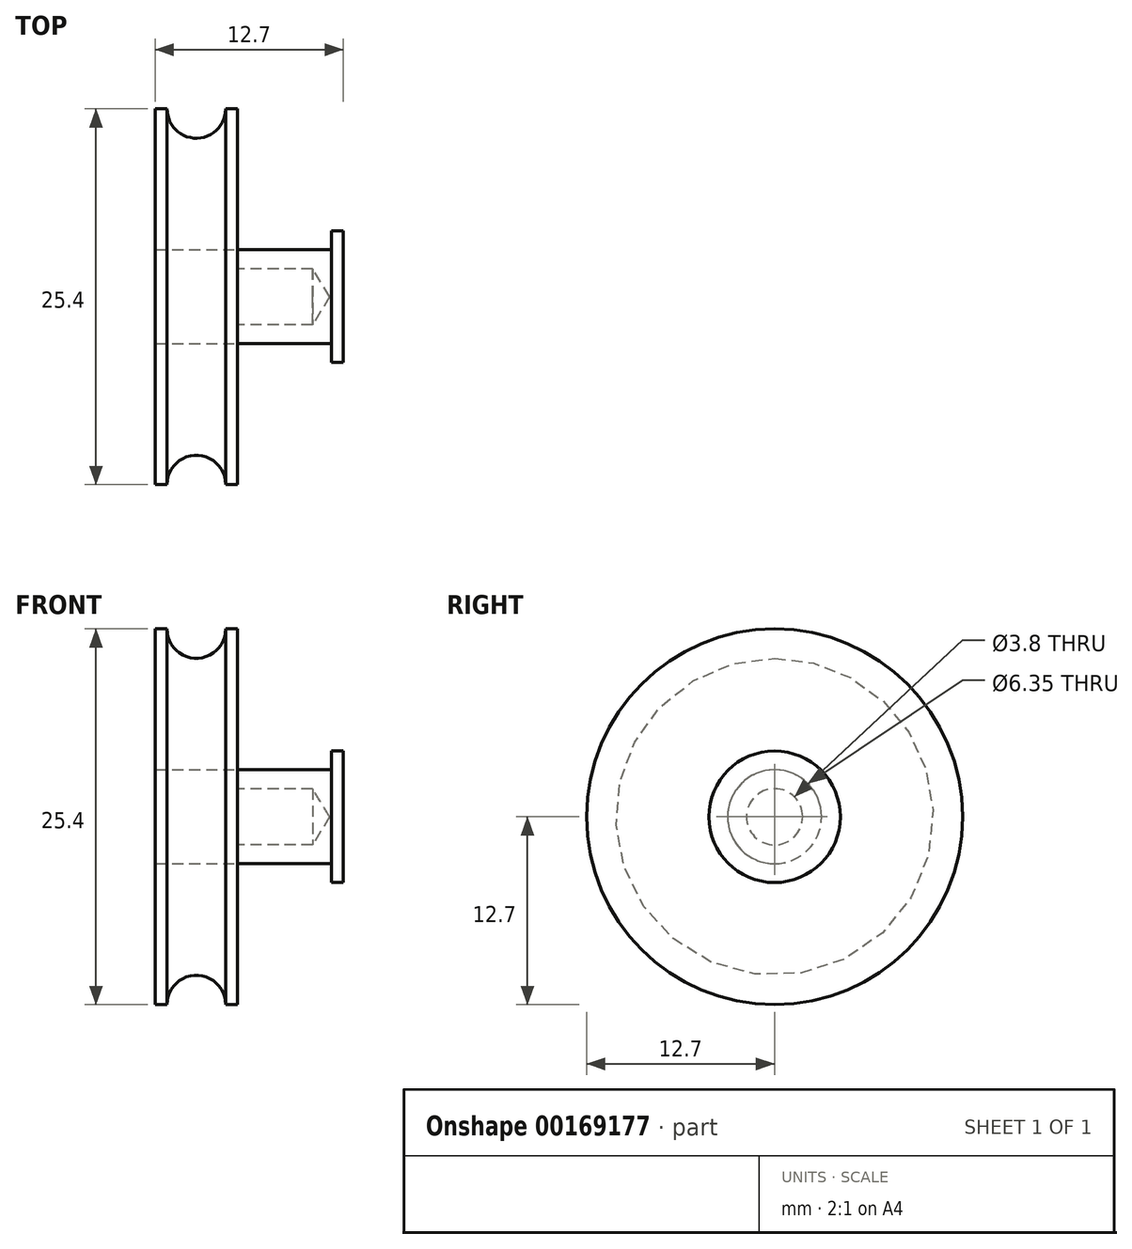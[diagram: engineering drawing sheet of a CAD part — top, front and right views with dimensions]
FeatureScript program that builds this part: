
annotation { "Feature Type Name" : "Feature", "Feature Type Description" : "" }
export const myFeature = defineFeature(function(context is Context, id is Id, definition is map)
    precondition{}
    {
        {
            var Q0;
            Q0=qCreatedBy(makeId("Front.planeOp"),FACE);
            var sketch = newSketch(context, id + "F0", { "sketchPlane" : qUnion([Q0])});
            skLineSegment(sketch, "E0.bottom", {"start": v(0, 0) * mm, "end": v(5.56, 0) * mm});
            skLineSegment(sketch, "E0.top", {"start": v(0, 12.7) * mm, "end": v(0.8, 12.7) * mm});
            skLineSegment(sketch, "E0.left", {"start": v(0, 0) * mm, "end": v(0, 12.7) * mm});
            skLineSegment(sketch, "E0.right", {"start": v(5.56, 0) * mm, "end": v(5.56, 12.7) * mm});
            skLineSegment(sketch, "E1.trimOffspring", {"start": v(4.76, 12.7) * mm, "end": v(5.56, 12.7) * mm});
            skArc(sketch, "E2", {"start": v(0.8, 12.7) * mm, "mid": v(2.78, 10.72) * mm, "end": v(4.76, 12.7) * mm});
            skSolve(sketch);
        }
        {
            var Q0;
            Q0=makeQuery(id+"F0.imprint","IMPRINT",FACE,{"disambiguationData":[TD([[makeQuery(id+"F0.imprint","IMPRINT",EDGE,{"derivedFrom":sQuery(id+"F0.wireOp",EDGE,"E0.bottom")}),1.0]])]});
            var Q1;
            Q1=sQuery(id+"F0.wireOp",EDGE,"E0.bottom");
            revolve(context, id + "F1", {"entities" : qUnion([Q0]), "axis" : qUnion([Q1]), "revolveType" : RevolveType.FULL});
        }
        {
            var Q0;
            Q0=makeQuery(id+"F1.opRevolve","SWEPT_FACE",FACE,{"disambiguationData":[OSD([sQuery(id+"F0.wireOp",EDGE,"E0.right")])]});
            var sketch = newSketch(context, id + "F2", { "sketchPlane" : qUnion([Q0])});
            skCircle(sketch, "E3", {"center": v(0, 0) * mm, "radius": 3.18 * mm});
            skSolve(sketch);
        }
        {
            var Q0;
            Q0=makeQuery(id+"F2.imprint","IMPRINT",FACE,{"disambiguationData":[TD([[makeQuery(id+"F2.imprint","IMPRINT",EDGE,{"derivedFrom":sQuery(id+"F2.wireOp",EDGE,"E3")}),1.0]])]});
            extrude(context, id + "F3", {"entities" : qUnion([Q0]), "operationType" : NewBodyOperationType.REMOVE, "endBound" : BoundingType.UP_TO_NEXT, "oppositeDirection" : true, "depth" : 25.4 * mm});
        }
        {
            var Q0;
            Q0=makeQuery(id+"F2.imprint","IMPRINT",FACE,{"disambiguationData":[TD([[makeQuery(id+"F2.imprint","IMPRINT",EDGE,{"derivedFrom":sQuery(id+"F2.wireOp",EDGE,"E3")}),1.0]])]});
            extrude(context, id + "F4", {"entities" : qUnion([Q0]), "depth" : 6.35 * mm});
        }
        {
            var Q0;
            Q0=makeQuery(id+"F4.opExtrude","CAP_FACE",FACE,{"disambiguationData":[OSD([sQuery(id+"F2.wireOp",EDGE,"E3")])],"isStart":false});
            var sketch = newSketch(context, id + "F5", { "sketchPlane" : qUnion([Q0])});
            skCircle(sketch, "E4", {"center": v(0, 0) * mm, "radius": 4.45 * mm});
            skSolve(sketch);
        }
        {
            var Q0;
            Q0=makeQuery(id+"F5.imprint","IMPRINT",FACE,{"disambiguationData":[TD([[makeQuery(id+"F5.imprint","IMPRINT",EDGE,{"derivedFrom":sQuery(id+"F5.wireOp",EDGE,"E4")}),1.0]])]});
            var Q1;
            Q1=makeQuery(id+"F5.imprint","IMPRINT",FACE,{"disambiguationData":[TD([[makeQuery(id+"F5.imprint","IMPRINT",EDGE,{"derivedFrom":makeQuery(id+"F4.opExtrude","CAP_EDGE",EDGE,{"disambiguationData":[OSD([sQuery(id+"F2.wireOp",EDGE,"E3")])],"isStart":false})}),1.0]])]});
            extrude(context, id + "F6", {"entities" : qUnion([Q0, Q1]), "operationType" : NewBodyOperationType.ADD, "depth" : 0.8 * mm});
        }
        {
            var Q0;
            Q0=sQuery(id+"F2.wireOp",VERTEX,"E3.center");
            var Q1;
            Q1=makeQuery(id+"F4.opExtrude","SWEPT_BODY",BODY,{"disambiguationData":[OSD([sQuery(id+"F2.wireOp",EDGE,"E3")])]});
            hole(context, id + "F7", {"style" : HoleStyle.SIMPLE, "endStyle" : HoleEndStyle.BLIND, "oppositeDirection" : true, "standardTappedOrClearance" : lookupTablePath({ "standard" : "ANSI", "engagement" : "75%", "pitch" : "24 tpi", "size" : "#10", "type" : "Tapped" }), "standardBlindInLast" : lookupTablePath({ "standard" : "ANSI", "engagement" : "75%", "pitch" : "24 tpi", "size" : "#10", "type" : "Tapped" }), "holeDiameter" : 3.8 * mm, "holeDepth" : 5.08 * mm, "startFromSketch" : true, "locations" : qUnion([Q0]), "scope" : qUnion([Q1]), "majorDiameter" : 4.83 * mm});
        }
    });
